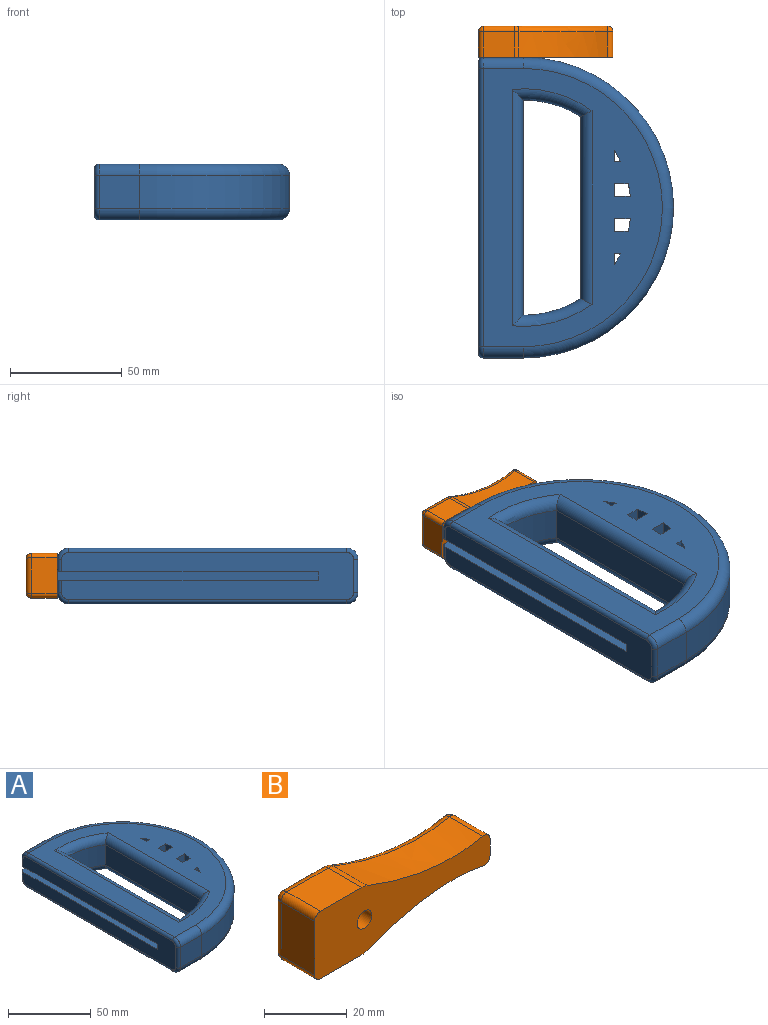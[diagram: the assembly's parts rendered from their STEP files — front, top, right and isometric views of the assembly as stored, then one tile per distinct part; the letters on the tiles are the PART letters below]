
ASSEMBLY  parts=2 mates=1
PART A: 55 faces, bbox 92.8x145.7x25.8 mm
  f0: plane 17.96x15mm, normal (0,1,0), area 224.8mm2, adj f9,f15,f20,f32,f40,f41,f42,f43
  f1: plane 25x5.55mm, normal (1,0,0), area 138.8mm2, adj f13,f14,f21,f29
  f2: cylinder r=48.18mm len=25mm, axis (0,0,-1), area 140.7mm2, adj f13,f14,f21,f29
  f3: plane 25x5.62mm, normal (1,0,0), area 140.4mm2, adj f13,f14,f27,f28
  f4: cylinder r=48.18mm len=25mm, axis (0,0,-1), area 143.1mm2, adj f13,f14,f22,f23
  f5: cylinder r=48.18mm len=25.79mm, axis (0,0,-1), area 408.3mm2, adj f8,f24,f36,f39
  f6: cylinder r=48.18mm len=25mm, axis (0,0,-1), area 145.2mm2, adj f13,f14,f25,f26
  f7: cylinder r=48.18mm len=25mm, axis (0,0,-1), area 142.4mm2, adj f13,f14,f27,f28
  f8: plane 96.37x15mm, normal (1,0,0), area 1445.5mm2, adj f5,f12,f35,f38
  f9: cylinder r=67.29mm len=134.58mm, axis (0,0,-1), area 3170.9mm2, adj f0,f11,f16,f19
  f10: plane 130.58x21mm, normal (-1,0,0), area 2275.2mm2, adj f40,f44,f45,f46,f47,f48,f49,f50
  f11: plane 17.96x15mm, normal (0,-1,0), area 269.4mm2, adj f9,f17,f18,f50
  f12: cylinder r=48.18mm len=25.79mm, axis (0,0,-1), area 408.3mm2, adj f8,f24,f34,f37
  f13: plane 124.58x80.25mm, normal (0,0,1), area 4629.2mm2, adj f1,f2,f3,f4,f6,f7,f15,f16
  f14: plane 124.58x80.25mm, normal (0,0,-1), area 4629.2mm2, adj f1,f2,f3,f4,f6,f7,f18,f19
  f15: cylinder r=5mm len=17.96mm, axis (1,0,0), area 141.1mm2, adj f0,f13,f16,f47
  f16: torus R=62.29mm, axis (0,0,1), area 1615.5mm2, adj f9,f13,f15,f17
  f17: cylinder r=5mm len=17.96mm, axis (-1,0,0), area 141.1mm2, adj f11,f13,f16,f49
  f18: cylinder r=5mm len=17.96mm, axis (1,0,0), area 141.1mm2, adj f11,f14,f19,f51
  f19: torus R=62.29mm, axis (0,0,1), area 1615.5mm2, adj f9,f14,f18,f20
  f20: cylinder r=5mm len=17.96mm, axis (-1,0,0), area 141.1mm2, adj f0,f14,f19,f53
  f21: plane 25x6.2mm, normal (0,-1,0), area 155mm2, adj f1,f2,f13,f14
  f22: plane 25x2.75mm, normal (0,1,0), area 68.8mm2, adj f4,f13,f14,f23
  f23: plane 25x5.02mm, normal (1,0,0), area 125.4mm2, adj f4,f13,f14,f22
  f24: plane 81.39x15mm, normal (-1,0,0), area 1220.9mm2, adj f5,f12,f30,f31
  f25: plane 25x5.09mm, normal (1,0,0), area 127.3mm2, adj f6,f13,f14,f26
  f26: plane 25x2.79mm, normal (0,-1,0), area 69.7mm2, adj f6,f13,f14,f25
  f27: plane 25x6.22mm, normal (0,1,0), area 155.5mm2, adj f3,f7,f13,f14
  f28: plane 25x7.13mm, normal (0,-1,0), area 178.4mm2, adj f3,f7,f13,f14
  f29: plane 25x7.12mm, normal (0,1,0), area 178mm2, adj f1,f2,f13,f14
  f30: cylinder r=5mm len=86.72mm, axis (0,-1,0), area 654.6mm2, adj f14,f24,f34,f36
  f31: cylinder r=5mm len=86.72mm, axis (0,1,0), area 654.6mm2, adj f13,f24,f37,f39
  f32: cylinder r=2.5mm len=5mm, axis (0,-1,0), area 78.5mm2, adj f0,f33
  f33: plane 5x5mm, normal (0,1,0), area 19.6mm2, adj f32
  f34: torus R=53.18mm, axis (0,0,1), area 244.1mm2, adj f12,f14,f30,f35
  f35: cylinder r=5mm len=105.89mm, axis (0,1,0), area 784.5mm2, adj f8,f14,f34,f36
  f36: torus R=53.18mm, axis (0,0,1), area 244.1mm2, adj f5,f14,f30,f35
  f37: torus R=53.18mm, axis (0,0,1), area 244.1mm2, adj f12,f13,f31,f38
  f38: cylinder r=5mm len=105.89mm, axis (0,-1,0), area 784.5mm2, adj f8,f13,f37,f39
  f39: torus R=53.18mm, axis (0,0,1), area 244.1mm2, adj f5,f13,f31,f38
  f40: plane 116.8x5mm, normal (0,0,-1), area 583.1mm2, adj f0,f10,f41,f45,f46
  f41: plane 116.8x2.12mm, normal (0.71,0,-0.71), area 350.4mm2, adj f0,f40,f42,f45
  f42: plane 116.8x8.24mm, normal (-1,0,0), area 962.7mm2, adj f0,f41,f43,f45
  f43: plane 116.8x2.12mm, normal (0.71,0,0.71), area 350.4mm2, adj f0,f42,f44,f45
  f44: plane 116.8x5mm, normal (0,0,1), area 583.1mm2, adj f0,f10,f43,f45,f54
  f45: plane 8.24x7.12mm, normal (0,1,0), area 33mm2, adj f10,f40,f41,f42,f43,f44
  f46: cylinder r=2mm len=5.5mm, axis (0,0,-1), area 17.3mm2, adj f0,f10,f40,f47
  f47: torus R=3mm, axis (1,0,0), area 21.1mm2, adj f10,f15,f46,f48
  f48: cylinder r=2mm len=124.58mm, axis (0,1,0), area 391.4mm2, adj f10,f13,f47,f49
  f49: torus R=3mm, axis (1,0,0), area 21.1mm2, adj f10,f17,f48,f50
  f50: cylinder r=2mm len=15mm, axis (0,0,-1), area 47.1mm2, adj f10,f11,f49,f51
  f51: torus R=3mm, axis (1,0,0), area 21.1mm2, adj f10,f18,f50,f52
  f52: cylinder r=2mm len=124.58mm, axis (0,-1,0), area 391.4mm2, adj f10,f14,f51,f53
  f53: torus R=3mm, axis (1,0,0), area 21.1mm2, adj f10,f20,f52,f54
  f54: cylinder r=2mm len=5.5mm, axis (0,0,-1), area 17.3mm2, adj f0,f10,f44,f53
PART B: 28 faces, bbox 60.1x14x20.2 mm
  f0: plane 55.1x15mm, normal (0,1,0), area 427.7mm2, adj f16,f19,f20,f21,f22,f23,f24,f27
  f1: plane 60.09x20mm, normal (0,-1,0), area 756.4mm2, adj f2,f3,f4,f5,f7,f8,f9,f10
  f2: plane 11.5x4.92mm, normal (1,0,0), area 56.6mm2, adj f1,f9,f10,f27
  f3: plane 14.11x11.5mm, normal (0,0,1), area 162.3mm2, adj f1,f12,f15,f19
  f4: plane 14.11x11.5mm, normal (0,0,-1), area 162.3mm2, adj f1,f13,f14,f20
  f5: cylinder r=2.55mm len=5.1mm, axis (0,-1,0), area 80.1mm2, adj f1,f6
  f6: plane 5.1x5.1mm, normal (0,-1,0), area 20.4mm2, adj f5
  f7: extruded ~39.7x11.5mm, area 467.2mm2, adj f1,f10,f15,f23
  f8: extruded ~39.7x11.5mm, area 467.2mm2, adj f1,f9,f14,f24
  f9: cylinder r=2mm len=11.5mm, axis (0,1,0), area 41mm2, adj f1,f2,f8,f26
  f10: cylinder r=2mm len=11.5mm, axis (0,1,0), area 41mm2, adj f1,f2,f7,f25
  f11: plane 16x11.5mm, normal (-1,0,0), area 184mm2, adj f1,f12,f13,f16
  f12: cylinder r=2mm len=11.5mm, axis (0,1,0), area 36.1mm2, adj f1,f3,f11,f17
  f13: cylinder r=2mm len=11.5mm, axis (0,-1,0), area 36.1mm2, adj f1,f4,f11,f18
  f14: cylinder r=5mm len=11.5mm, axis (0,1,0), area 21.9mm2, adj f1,f4,f8,f22
  f15: cylinder r=5mm len=11.5mm, axis (0,1,0), area 21.9mm2, adj f1,f3,f7,f21
  f16: cylinder r=2.5mm len=16mm, axis (0,0,1), area 60.9mm2, adj f0,f11,f17,f18
  f17: bspline ~2.65x2.5mm, area 5.5mm2, adj f12,f16,f19
  f18: bspline ~2.65x2.5mm, area 5.5mm2, adj f13,f16,f20
  f19: cylinder r=2.5mm len=14.11mm, axis (1,0,0), area 54.4mm2, adj f0,f3,f17,f21
  f20: cylinder r=2.5mm len=14.11mm, axis (-1,0,0), area 54.4mm2, adj f0,f4,f18,f22
  f21: torus R=2.5mm, axis (0,-1,0), area 6.1mm2, adj f0,f15,f19,f23
  f22: torus R=2.5mm, axis (0,-1,0), area 6.1mm2, adj f0,f14,f20,f24
  f23: bspline ~42.12x8.94mm, area 160.5mm2, adj f0,f7,f21,f25
  f24: bspline ~42.12x8.94mm, area 160.5mm2, adj f0,f8,f22,f26
  f25: bspline ~3.39x3.08mm, area 6.9mm2, adj f10,f23,f27
  f26: bspline ~3.39x3.08mm, area 6.9mm2, adj f9,f24,f27
  f27: cylinder r=2.5mm len=4.92mm, axis (0,0,-1), area 16.9mm2, adj f0,f2,f25,f26
PLACE A t=(411.98,120.84,341.35)mm fixed
PLACE B rot(axis=(0,1,0),0.6deg) t=(376.99,188.06,431.54)mm
MATE revolute B.f5 <-> A.f32  axis (0,-1,0) through (386.11,193.06,341.35)mm
